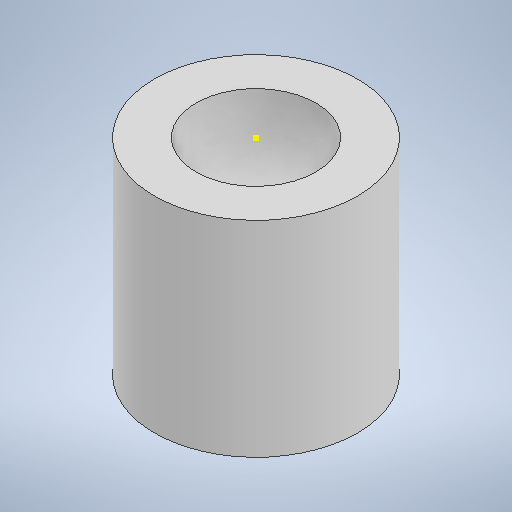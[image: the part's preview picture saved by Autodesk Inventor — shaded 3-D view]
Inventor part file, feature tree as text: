
AUTODESK INVENTOR PART (.ipt)
format: ipt  version: 2025.2 (Build 292293000, 293)  size: 216,576 bytes
history: native  units: in
note: dims shown in document units (in); Inventor stores cm internally (conversion verified against a paired STEP export)
features: sketch x5, extrude x2, revolve x1
ambient origin geometry x8: Origin, YZ Plane, XZ Plane, XY Plane, X Axis, Y Axis, Z Axis, Center Point
bodies: Solid1 (feature_tree)
feature tree (8):
  sketch  "Sketch1"  dims[d0=0.7006in d1=0.5824in]
  extrude  "Extrusion1"  Depth=0.5824in
  extrude  "Extrusion2"  Depth=0.3937in TaperAngle=0.0deg
  revolve  "Revolution1"  Angle=360.0deg
  sketch  "Sketch5"
  sketch  "Sketch2"  dims[d2=0.315in d3=0.0in d4=0.3937in d5=0.0in]
  sketch  "Sketch3"  dims[d6=0.4134in d7=360.0deg]
  sketch  "Sketch4"
